# Revit family: Chair-Soft_Seating-Allermuir-Fifty Series-Armchair
name_source: partatom
category: Furniture
revit_build: Autodesk Revit Architecture 2012 (Build: 20110309_2315(x64)
units: mm (PartAtom-declared; Revit-internal decimal feet)

## types (2) — shared parameters
04 CSI = 12 51 00
95 CSI = 12510
Arm Height = 2' - 1 151/256"
Assembly Code = E2020200
Brochure URL = http://www.allermuir.net
CAD Blocks URL = http://www.allermuir.net
Color Availability = See price list for material options
Cushion Material = Fabric - Allermuir - Silcoates
Description = Armchair
Fabric Spec Sheets = http://www.allermuir.net
LEED Stats URL = http://www.allermuir.net
Leg Base Material = Plastic - Allermuir - Black
Leg Materials = Metal - Allermuir - Chrome - Polished
Manufacturer = Allermuir
Manufacturer Fax = (419) 887 5805
Overall Depth = 2' - 3 143/256"
Overall Height = 2' - 6 79/256"
Overall Width = 2' - 3 143/256"
Pedestal Base = No
Plugin Data URL = http://products.ecoscorecard.com
Pricing URL = http://www.allermuir.net
Product Line = Fifty Series
Product Page URL = http://www.allermuir.net
Seat Depth = 1' - 6"
Seat Height = 1' - 6 1/2"
Seat Width = 1' - 9 83/128"
Specifications URL = http://www.allermuir.net
Subcategory = Soft Seating
Swaged Tubular Steel Legs = not(Pedestal Base)
URL = http://www.allermuir.net
Weight = 0.0 lb
ecoScorecard Product Page = http://products.ecoscorecard.com
ecoScorecard_data = http://thesenatorgroup.ecoscorecard.com

## per-type parameters (varying)
| type | Base | Legs | Model |
| FIFT01 - Armchair | No | Yes | FIFT01 |
| FIFT04 - Armchair | Yes | No | FIFT04 |

## geometry (parser evidence)
native form markers: Sweep x3
no freeform markers — native parametric forms only
